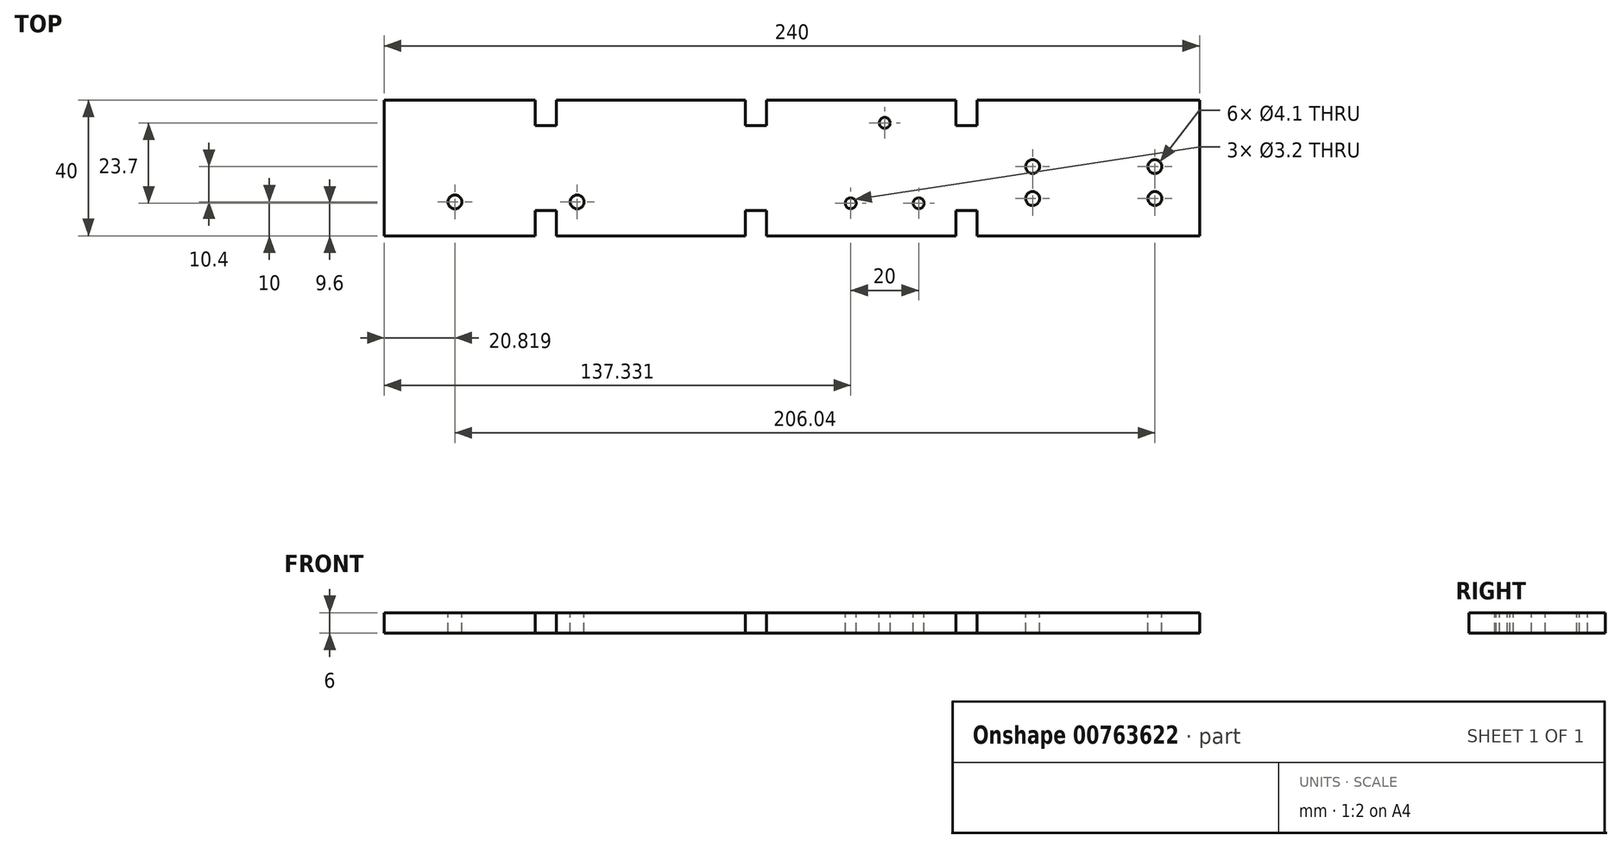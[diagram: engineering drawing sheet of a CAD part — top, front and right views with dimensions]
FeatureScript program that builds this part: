
annotation { "Feature Type Name" : "Feature", "Feature Type Description" : "" }
export const myFeature = defineFeature(function(context is Context, id is Id, definition is map)
    precondition{}
    {
        {
            var Q0;
            Q0=qCreatedBy(makeId("Top.planeOp"),FACE);
            var sketch = newSketch(context, id + "F0", { "sketchPlane" : qUnion([Q0])});
            skLineSegment(sketch, "E0.bottom", {"start": v(130.53, -20) * mm, "end": v(-109.47, -20) * mm});
            skLineSegment(sketch, "E0.top", {"start": v(130.53, 20) * mm, "end": v(-109.47, 20) * mm});
            skLineSegment(sketch, "E0.left", {"start": v(130.53, -20) * mm, "end": v(130.53, 20) * mm});
            skLineSegment(sketch, "E0.right", {"start": v(-109.47, -20) * mm, "end": v(-109.47, 20) * mm});
            skPoint(sketch, "E0.middle", {"position": v(10.53, 0) * mm});
            skSolve(sketch);
        }
        {
            var Q0;
            Q0 = qSketchRegion(id + "F0", true);
            extrude(context, id + "F1", {"entities" : qUnion([Q0]), "depth" : 6 * mm, "offsetDistance" : 25 * mm});
        }
        {
            var Q0;
            Q0=makeQuery(id+"F1.opExtrude","CAP_FACE",FACE,{"disambiguationData":[OSD([sQuery(id+"F0.wireOp",EDGE,"E0.bottom"),sQuery(id+"F0.wireOp",EDGE,"E0.top"),sQuery(id+"F0.wireOp",EDGE,"E0.left"),sQuery(id+"F0.wireOp",EDGE,"E0.right")])],"isStart":false});
            var sketch = newSketch(context, id + "F2", { "sketchPlane" : qUnion([Q0])});
            skLineSegment(sketch, "E1.bottom", {"start": v(65, -15) * mm, "end": v(-65, -15) * mm, "construction": true});
            skLineSegment(sketch, "E1.top", {"start": v(65, 15) * mm, "end": v(-65, 15) * mm, "construction": true});
            skLineSegment(sketch, "E1.left", {"start": v(65, -15) * mm, "end": v(65, 15) * mm, "construction": true});
            skLineSegment(sketch, "E1.right", {"start": v(-65, -15) * mm, "end": v(-65, 15) * mm, "construction": true});
            skPoint(sketch, "E1.middle", {"position": v(0, 0) * mm});
            skLineSegment(sketch, "E2", {"start": v(-65, 0) * mm, "end": v(65, 0) * mm, "construction": true});
            skLineSegment(sketch, "E3", {"start": v(0, 15) * mm, "end": v(0, -15) * mm, "construction": true});
            skLineSegment(sketch, "E4.bottom", {"start": v(-3.1, -20) * mm, "end": v(3.1, -20) * mm});
            skLineSegment(sketch, "E4.top", {"start": v(-3.1, -12.5) * mm, "end": v(3.1, -12.5) * mm});
            skLineSegment(sketch, "E4.left", {"start": v(-3.1, -20) * mm, "end": v(-3.1, -12.5) * mm});
            skLineSegment(sketch, "E4.right", {"start": v(3.1, -20) * mm, "end": v(3.1, -12.5) * mm});
            skPoint(sketch, "E5", {"position": v(0, -12.5) * mm});
            skLineSegment(sketch, "E6.bottom", {"start": v(-65, -20) * mm, "end": v(-58.8, -20) * mm});
            skLineSegment(sketch, "E6.top", {"start": v(-65, -12.5) * mm, "end": v(-58.8, -12.5) * mm});
            skLineSegment(sketch, "E6.left", {"start": v(-65, -20) * mm, "end": v(-65, -12.5) * mm});
            skLineSegment(sketch, "E6.right", {"start": v(-58.8, -20) * mm, "end": v(-58.8, -12.5) * mm});
            skLineSegment(sketch, "E7.bottom", {"start": v(58.8, -20) * mm, "end": v(65, -20) * mm});
            skLineSegment(sketch, "E7.top", {"start": v(58.8, -12.5) * mm, "end": v(65, -12.5) * mm});
            skLineSegment(sketch, "E7.left", {"start": v(58.8, -20) * mm, "end": v(58.8, -12.5) * mm});
            skLineSegment(sketch, "E7.right", {"start": v(65, -20) * mm, "end": v(65, -12.5) * mm});
            skLineSegment(sketch, "E8.MirrorCS", {"start": v(3.1, 20) * mm, "end": v(3.1, 12.5) * mm});
            skLineSegment(sketch, "E9.MirrorCS", {"start": v(-3.1, 20) * mm, "end": v(-3.1, 12.5) * mm});
            skLineSegment(sketch, "E10.MirrorCS", {"start": v(-58.8, 20) * mm, "end": v(-58.8, 12.5) * mm});
            skLineSegment(sketch, "E11.MirrorCS", {"start": v(65, 20) * mm, "end": v(65, 12.5) * mm});
            skLineSegment(sketch, "E12.MirrorCS", {"start": v(58.8, 20) * mm, "end": v(58.8, 12.5) * mm});
            skLineSegment(sketch, "E13.MirrorCS", {"start": v(-65, 20) * mm, "end": v(-65, 12.5) * mm});
            skLineSegment(sketch, "E14.MirrorCS", {"start": v(-3.1, 12.5) * mm, "end": v(3.1, 12.5) * mm});
            skLineSegment(sketch, "E15.MirrorCS", {"start": v(-65, 12.5) * mm, "end": v(-58.8, 12.5) * mm});
            skLineSegment(sketch, "E16.MirrorCS", {"start": v(-65, 20) * mm, "end": v(-58.8, 20) * mm});
            skLineSegment(sketch, "E17.MirrorCS", {"start": v(58.8, 12.5) * mm, "end": v(65, 12.5) * mm});
            skPoint(sketch, "E18.MirrorP", {"position": v(0, 12.5) * mm});
            skLineSegment(sketch, "E19.MirrorCS", {"start": v(58.8, 20) * mm, "end": v(65, 20) * mm});
            skLineSegment(sketch, "E20.MirrorCS", {"start": v(-3.1, 20) * mm, "end": v(3.1, 20) * mm});
            skSolve(sketch);
        }
        {
            var Q0;
            Q0 = qSketchRegion(id + "F2", true);
            var Q1;
            Q1=makeQuery(id+"F1.opExtrude","CAP_FACE",FACE,{"disambiguationData":[OSD([sQuery(id+"F0.wireOp",EDGE,"E0.bottom"),sQuery(id+"F0.wireOp",EDGE,"E0.top"),sQuery(id+"F0.wireOp",EDGE,"E0.left"),sQuery(id+"F0.wireOp",EDGE,"E0.right")])],"isStart":true});
            extrude(context, id + "F3", {"entities" : qUnion([Q0]), "operationType" : NewBodyOperationType.REMOVE, "endBound" : BoundingType.UP_TO_SURFACE, "oppositeDirection" : true, "depth" : 25 * mm, "endBoundEntityFace" : qUnion([Q1]), "offsetDistance" : 25 * mm});
        }
        {
            var Q0;
            Q0=makeQuery(id+"F1.opExtrude","CAP_FACE",FACE,{"disambiguationData":[OSD([sQuery(id+"F0.wireOp",EDGE,"E0.bottom"),sQuery(id+"F0.wireOp",EDGE,"E0.top"),sQuery(id+"F0.wireOp",EDGE,"E0.left"),sQuery(id+"F0.wireOp",EDGE,"E0.right")])],"isStart":false});
            var sketch = newSketch(context, id + "F4", { "sketchPlane" : qUnion([Q0])});
            skCircle(sketch, "E21", {"center": v(27.86, -10.4) * mm, "radius": 1.6 * mm});
            skCircle(sketch, "E22", {"center": v(47.86, -10.4) * mm, "radius": 1.6 * mm});
            skCircle(sketch, "E23", {"center": v(37.86, 13.3) * mm, "radius": 1.6 * mm});
            skLineSegment(sketch, "E24", {"start": v(27.86, -10.4) * mm, "end": v(47.86, -10.4) * mm, "construction": true});
            skPoint(sketch, "E25", {"position": v(37.86, -10.4) * mm});
            skLineSegment(sketch, "E26", {"start": v(37.86, -10.4) * mm, "end": v(37.86, 13.3) * mm, "construction": true});
            skPoint(sketch, "E27", {"position": v(37.86, 1.45) * mm});
            skLineSegment(sketch, "E28.bottom", {"start": v(52.46, -15) * mm, "end": v(23.26, -15) * mm, "construction": true});
            skLineSegment(sketch, "E28.top", {"start": v(52.46, 17.9) * mm, "end": v(23.26, 17.9) * mm, "construction": true});
            skLineSegment(sketch, "E28.left", {"start": v(52.46, -15) * mm, "end": v(52.46, 17.9) * mm, "construction": true});
            skLineSegment(sketch, "E28.right", {"start": v(23.26, -15) * mm, "end": v(23.26, 17.9) * mm, "construction": true});
            skSolve(sketch);
        }
        {
            var Q0;
            Q0=makeQuery(id+"F1.opExtrude","CAP_FACE",FACE,{"disambiguationData":[OSD([sQuery(id+"F0.wireOp",EDGE,"E0.bottom"),sQuery(id+"F0.wireOp",EDGE,"E0.top"),sQuery(id+"F0.wireOp",EDGE,"E0.left"),sQuery(id+"F0.wireOp",EDGE,"E0.right")])],"isStart":false});
            var sketch = newSketch(context, id + "F5", { "sketchPlane" : qUnion([Q0])});
            skCircle(sketch, "E29", {"center": v(-88.65, -10) * mm, "radius": 2.05 * mm});
            skCircle(sketch, "E30", {"center": v(-52.65, -10) * mm, "radius": 2.05 * mm});
            skLineSegment(sketch, "E31", {"start": v(-52.65, -10) * mm, "end": v(-88.65, -10) * mm, "construction": true});
            skLineSegment(sketch, "E32.bottom", {"start": v(-95.15, -13) * mm, "end": v(-46.15, -13) * mm, "construction": true});
            skLineSegment(sketch, "E32.top", {"start": v(-95.15, 66) * mm, "end": v(-46.15, 66) * mm, "construction": true});
            skLineSegment(sketch, "E32.left", {"start": v(-95.15, -13) * mm, "end": v(-95.15, 66) * mm, "construction": true});
            skLineSegment(sketch, "E32.right", {"start": v(-46.15, -13) * mm, "end": v(-46.15, 66) * mm, "construction": true});
            skLineSegment(sketch, "E33", {"start": v(-70.65, -13) * mm, "end": v(-70.65, 66) * mm, "construction": true});
            skLineSegment(sketch, "E34", {"start": v(-46.15, 26.5) * mm, "end": v(-95.15, 26.5) * mm, "construction": true});
            skPoint(sketch, "E35", {"position": v(-70.65, -10) * mm});
            skCircle(sketch, "E36", {"center": v(-88.65, -10) * mm, "radius": 6.25 * mm, "construction": true});
            skSolve(sketch);
        }
        {
            var Q0;
            Q0=makeQuery(id+"F1.opExtrude","CAP_FACE",FACE,{"disambiguationData":[OSD([sQuery(id+"F0.wireOp",EDGE,"E0.bottom"),sQuery(id+"F0.wireOp",EDGE,"E0.top"),sQuery(id+"F0.wireOp",EDGE,"E0.left"),sQuery(id+"F0.wireOp",EDGE,"E0.right")])],"isStart":false});
            var sketch = newSketch(context, id + "F6", { "sketchPlane" : qUnion([Q0])});
            skCircle(sketch, "E37", {"center": v(81.39, -9) * mm, "radius": 2.05 * mm});
            skCircle(sketch, "E38", {"center": v(117.39, -9) * mm, "radius": 2.05 * mm});
            skLineSegment(sketch, "E39", {"start": v(117.39, -9) * mm, "end": v(81.39, -9) * mm, "construction": true});
            skLineSegment(sketch, "E40.bottom", {"start": v(71.89, -13) * mm, "end": v(126.89, -13) * mm, "construction": true});
            skLineSegment(sketch, "E40.top", {"start": v(71.89, 68.7) * mm, "end": v(126.89, 68.7) * mm, "construction": true});
            skLineSegment(sketch, "E40.left", {"start": v(71.89, -13) * mm, "end": v(71.89, 68.7) * mm, "construction": true});
            skLineSegment(sketch, "E40.right", {"start": v(126.89, -13) * mm, "end": v(126.89, 68.7) * mm, "construction": true});
            skLineSegment(sketch, "E41", {"start": v(99.39, -13) * mm, "end": v(99.39, 68.7) * mm, "construction": true});
            skLineSegment(sketch, "E42", {"start": v(126.89, 27.85) * mm, "end": v(71.89, 27.85) * mm, "construction": true});
            skPoint(sketch, "E43", {"position": v(99.39, -9) * mm});
            skCircle(sketch, "E44", {"center": v(81.39, 0.4) * mm, "radius": 2.05 * mm});
            skCircle(sketch, "E45", {"center": v(117.39, 0.4) * mm, "radius": 2.05 * mm});
            skLineSegment(sketch, "E46", {"start": v(81.39, -9) * mm, "end": v(81.39, 0.4) * mm, "construction": true});
            skLineSegment(sketch, "E47", {"start": v(117.39, 0.4) * mm, "end": v(117.39, -9) * mm, "construction": true});
            skSolve(sketch);
        }
        {
            var Q0;
            Q0 = qSketchRegion(id + "F4", true);
            var Q1;
            Q1 = qSketchRegion(id + "F5", true);
            var Q2;
            Q2 = qSketchRegion(id + "F6", true);
            extrude(context, id + "F7", {"entities" : qUnion([Q0, Q1, Q2]), "operationType" : NewBodyOperationType.REMOVE, "endBound" : BoundingType.THROUGH_ALL, "oppositeDirection" : true, "depth" : 25 * mm, "offsetDistance" : 25 * mm});
        }
        {
            var Q0;
            Q0 = qSketchRegion(id + "F6", true);
            var Q1;
            Q1 = qSketchRegion(id + "F5", true);
            var Q2;
            Q2 = qSketchRegion(id + "F4", true);
            extrude(context, id + "F8", {"entities" : qUnion([Q0, Q1, Q2]), "operationType" : NewBodyOperationType.REMOVE, "endBound" : BoundingType.THROUGH_ALL, "oppositeDirection" : true, "depth" : 25 * mm, "offsetDistance" : 25 * mm});
        }
    });
